# Revit family: 2840_Intrinsically Safe Analog Smoke Detector
name_source: partatom
category: Fire Alarm Devices
units: mm (PartAtom-declared; Revit-internal decimal feet)

## family parameters
Cut with Voids When Loaded = No
Host = Face
Maintain Annotation Orientation = No
OmniClass Number = 23.85.30.21
OmniClass Title = Environmental Detection/Registration
Part Type = Normal
Room Calculation Point = No
Round Connector Dimension = Use Diameter
Shared = No

## types (2) — shared parameters
ATEX Certificate = DEKRA 11ATEX0107
ATEX Clasification = II 1 G Ex ia IIC T5 Ga
Ambient Humidity = Maximum 95 % RH
Ambient Temperature Operating = -10 to +55 °C
Ambient Temperature Storage = -25 to +70 °C
CPR = 2831-CPR-F2748
Clearance Area = Clearance Area
Current (Active) = ≤ 1.5 mA
Current Quiescent = ≤ 0.3 mA
H_Detector (mm) = 62 mm  [stored 0.203412 ft]
Manufacturer = Panasonic
Max_Wire Size = Ø 1.75 mm (2.5 mm²)
Min_Wire Size = Ø 0.35 mm (0.08 mm²)
Model = 2840
Omniclass Code = 23.85.30.21.11.11.11
Omniclass Description = Smoke Detectors
Product Material = FR ABS and polycarbonate_Panasonic_Grey
Tested and Approved = EN54-7
Type Comments = The intrinsically safe analog photoelectric 2840 is used inside hazardous (Ex) areas. The detector is connected to the IS barrier unit 2842 via the IS COM line. The detector can be mounted with or without the water-proof IS back-box 2843.
URL = https://www.panasonic-fire-security.com
Uniclass 2015 Code = Pr_75_80_30_27
Uniclass 2015 Description = Fire and smoke detector bases
Uniformat 2010  Code = D7050
Uniformat 2010 Description = Detection and Alarm
Version = RVT20
Voltage Allowed = 15 - 17.3 VDC
Voltage Normal = 16 VDC
Weight = 300g
Zone Classification = Zone 0 / 1 / 2
zero-valued in all types: Default Elevation

## per-type parameters (varying)
| type | Base | Description | H_Base (mm) | H_Total (mm) | Ingress Protection Rating | ø (mm) |
| 2840 | No | Intrinsically safe analog photoelectric smoke detector 2840 | 0 mm  [stored 0 ft] | 62 mm  [stored 0.203412 ft] | IP22 | 102 mm |
| 2840_2843 | Yes | Intrinsically safe analog photoelectric smoke detector 2840 with back-box 2843 | 58 mm  [stored 0.190289 ft] | 100 mm  [stored 0.328084 ft] | IP44 | 110 mm  [stored 0.360892 ft] |

note: [stored X ft] marks values corroborated as IEEE doubles in the binary element streams (Revit-internal decimal feet)

## geometry (parser evidence)
native form markers: Blend x87, Sweep x8
no freeform markers — native parametric forms only
